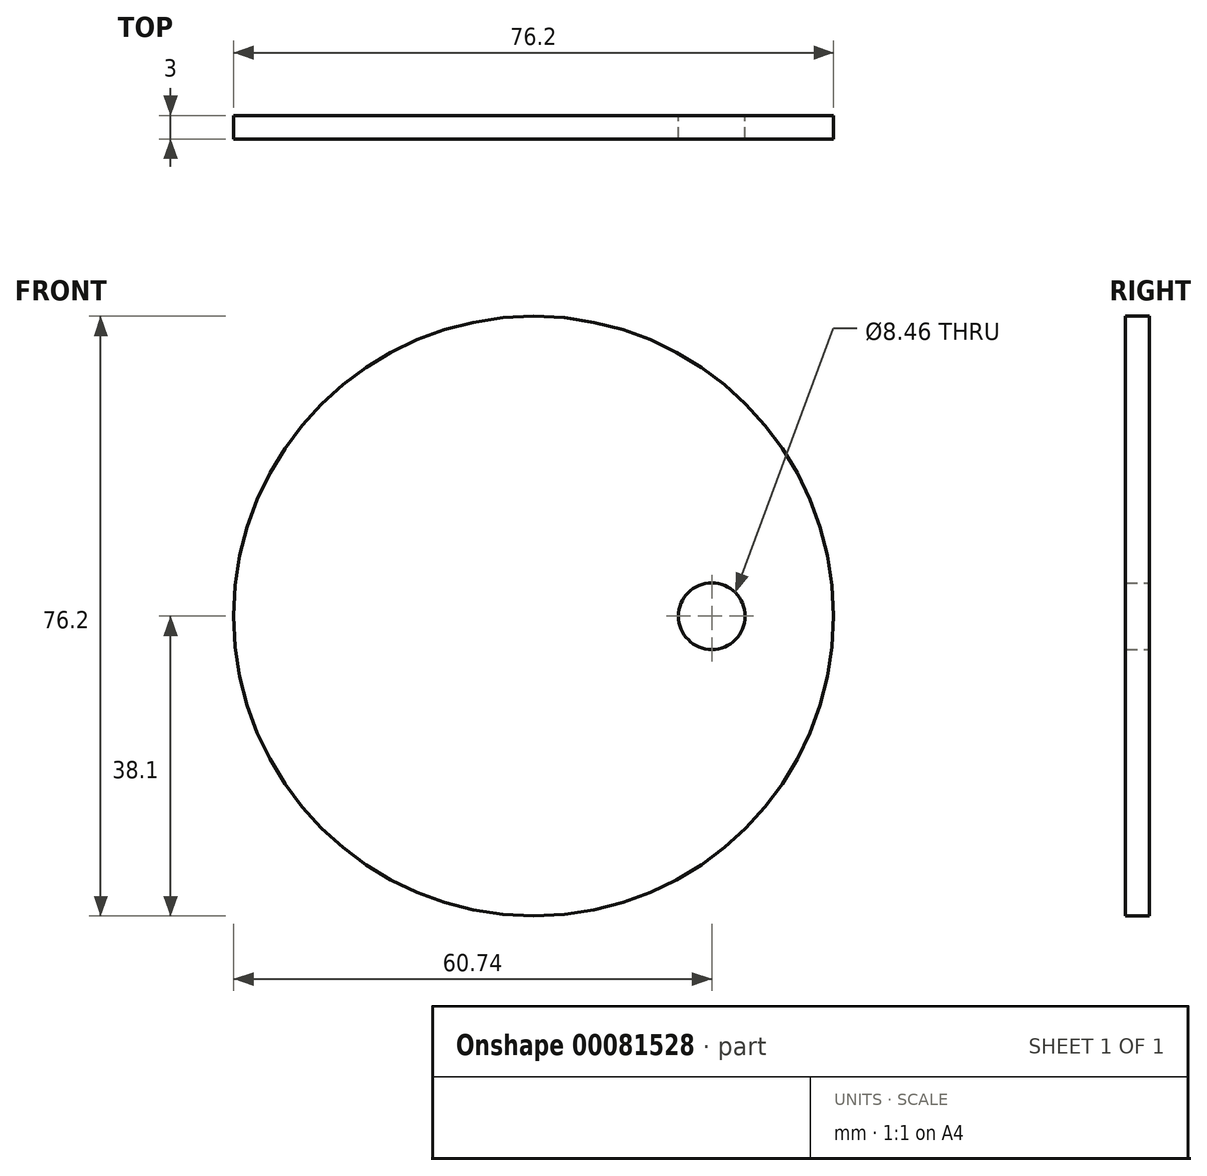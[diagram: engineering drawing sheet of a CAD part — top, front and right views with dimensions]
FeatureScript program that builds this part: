
annotation { "Feature Type Name" : "Feature", "Feature Type Description" : "" }
export const myFeature = defineFeature(function(context is Context, id is Id, definition is map)
    precondition{}
    {
        {
            var Q0;
            Q0=qCreatedBy(makeId("Front.planeOp"),FACE);
            var sketch = newSketch(context, id + "F0", { "sketchPlane" : qUnion([Q0])});
            skCircle(sketch, "E0", {"center": v(0, 0) * mm, "radius": 38.1 * mm});
            skCircle(sketch, "E1", {"center": v(22.64, 0) * mm, "radius": 4.23 * mm});
            skSolve(sketch);
        }
        {
            var Q0;
            Q0 = qSketchRegion(id + "F0", true);
            extrude(context, id + "F1", {"entities" : qUnion([Q0]), "depth" : 3 * mm});
        }
    });
